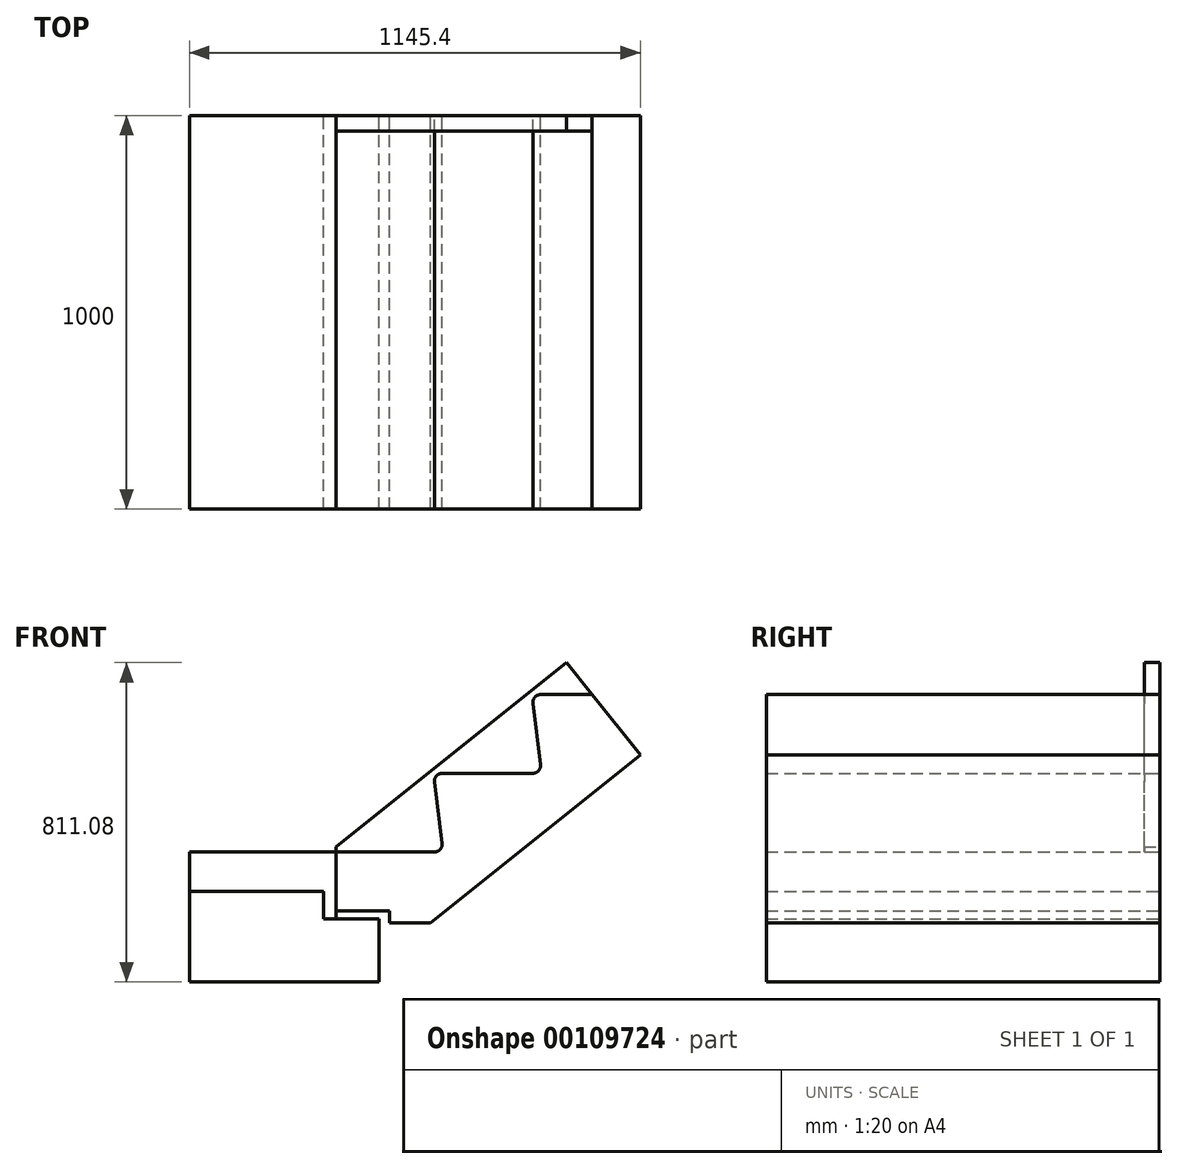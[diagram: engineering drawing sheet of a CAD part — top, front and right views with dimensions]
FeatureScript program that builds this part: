
annotation { "Feature Type Name" : "Feature", "Feature Type Description" : "" }
export const myFeature = defineFeature(function(context is Context, id is Id, definition is map)
    precondition{}
    {
        {
            var Q0;
            Q0=qCreatedBy(makeId("Front.planeOp"),FACE);
            var sketch = newSketch(context, id + "F0", { "sketchPlane" : qUnion([Q0])});
            skLineSegment(sketch, "E0", {"start": v(-200.38, -23.77) * mm, "end": v(49.16, -23.77) * mm});
            skLineSegment(sketch, "E1", {"start": v(69, -1.3) * mm, "end": v(49.62, 153.75) * mm});
            skLineSegment(sketch, "E2", {"start": v(-200.38, -11.26) * mm, "end": v(385.33, 457.31) * mm});
            skLineSegment(sketch, "E3", {"start": v(-90.79, -353.77) * mm, "end": v(-572.74, -353.77) * mm});
            skLineSegment(sketch, "E4", {"start": v(39.21, -203.77) * mm, "end": v(-63.95, -203.77) * mm});
            skLineSegment(sketch, "E5", {"start": v(69.47, 176.23) * mm, "end": v(299.16, 176.23) * mm});
            skLineSegment(sketch, "E6", {"start": v(319, 198.7) * mm, "end": v(299.62, 353.75) * mm});
            skLineSegment(sketch, "E7", {"start": v(319.47, 376.23) * mm, "end": v(450.15, 376.23) * mm});
            skLineSegment(sketch, "E8", {"start": v(-90.79, -193.77) * mm, "end": v(-90.79, -353.77) * mm});
            skLineSegment(sketch, "E9", {"start": v(-232.11, -193.77) * mm, "end": v(-232.11, -123.77) * mm});
            skLineSegment(sketch, "E10", {"start": v(-63.95, -173.77) * mm, "end": v(-200.38, -173.77) * mm});
            skLineSegment(sketch, "E11", {"start": v(-90.79, -193.77) * mm, "end": v(-232.11, -193.77) * mm});
            skLineSegment(sketch, "E12", {"start": v(-200.38, -173.77) * mm, "end": v(-200.38, -23.77) * mm});
            skLineSegment(sketch, "E13", {"start": v(318.48, 540.94) * mm, "end": v(688.52, 78.06) * mm});
            skLineSegment(sketch, "E14", {"start": v(-572.74, 82.67) * mm, "end": v(-572.74, -447.5) * mm});
            skArc(sketch, "E15", {"start": v(49.16, -23.77) * mm, "mid": v(64.15, -17) * mm, "end": v(69, -1.3) * mm});
            skArc(sketch, "E16", {"start": v(69.47, 176.23) * mm, "mid": v(54.48, 169.47) * mm, "end": v(49.62, 153.75) * mm});
            skArc(sketch, "E17", {"start": v(299.16, 176.23) * mm, "mid": v(314.15, 183) * mm, "end": v(319, 198.7) * mm});
            skArc(sketch, "E18", {"start": v(319.47, 376.23) * mm, "mid": v(304.48, 369.47) * mm, "end": v(299.62, 353.75) * mm});
            skLineSegment(sketch, "E19", {"start": v(-90.79, -353.77) * mm, "end": v(650.48, -353.77) * mm});
            skLineSegment(sketch, "E20", {"start": v(226.71, -53.77) * mm, "end": v(650.48, -53.77) * mm});
            skLineSegment(sketch, "E21", {"start": v(650.48, 14.5) * mm, "end": v(650.48, -397.5) * mm});
            skLineSegment(sketch, "E22", {"start": v(39.21, -203.77) * mm, "end": v(572.66, 222.99) * mm});
            skLineSegment(sketch, "E23", {"start": v(-90.79, -303.77) * mm, "end": v(-572.74, -303.77) * mm});
            skLineSegment(sketch, "E24", {"start": v(-63.95, -203.77) * mm, "end": v(-63.95, -173.77) * mm});
            skLineSegment(sketch, "E25", {"start": v(-232.11, -123.77) * mm, "end": v(-572.74, -123.77) * mm});
            skLineSegment(sketch, "E26", {"start": v(-200.38, -23.77) * mm, "end": v(-572.74, -23.77) * mm});
            skLineSegment(sketch, "E27", {"start": v(-200.38, -173.77) * mm, "end": v(-200.38, -193.77) * mm});
            skLineSegment(sketch, "E28", {"start": v(-90.79, -193.77) * mm, "end": v(-90.79, -173.77) * mm});
            skLineSegment(sketch, "E29", {"start": v(-200.38, -173.77) * mm, "end": v(-90.79, -193.77) * mm});
            skLineSegment(sketch, "E30", {"start": v(-90.79, -173.77) * mm, "end": v(-200.38, -193.77) * mm});
            skLineSegment(sketch, "E31", {"start": v(-200.38, -11.26) * mm, "end": v(-200.38, -23.77) * mm});
            skSolve(sketch);
        }
        {
            var Q0;
            {var subQ1=sQuery(id+"F0.wireOp",EDGE,"E9");Q0=makeQuery(id+"F0.imprint","IMPRINT",FACE,{"disambiguationData":[TD([[makeQuery(id+"F0.imprint","IMPRINT",EDGE,{"derivedFrom":subQ1}),1.0]])]});}
            var Q1;
            {var subQ0=sQuery(id+"F0.wireOp",EDGE,"E3");Q1=makeQuery(id+"F0.imprint","IMPRINT",FACE,{"disambiguationData":[TD([[makeQuery(id+"F0.imprint","IMPRINT",EDGE,{"derivedFrom":subQ0}),-1.0]])]});}
            extrude(context, id + "F1", {"entities" : qUnion([Q0, Q1]), "depth" : 1000 * mm});
        }
        {
            var Q0;
            {var subQ4=sQuery(id+"F0.wireOp",EDGE,"E9");Q0=makeQuery(id+"F0.imprint","IMPRINT",FACE,{"disambiguationData":[TD([[makeQuery(id+"F0.imprint","IMPRINT",EDGE,{"derivedFrom":subQ4}),-1.0]])]});}
            extrude(context, id + "F2", {"entities" : qUnion([Q0]), "depth" : 1000 * mm});
        }
        {
            var Q0;
            Q0=makeQuery(id+"F0.imprint","IMPRINT",FACE,{"disambiguationData":[TD([[makeQuery(id+"F0.imprint","IMPRINT",EDGE,{"derivedFrom":sQuery(id+"F0.wireOp",EDGE,"E0")}),-1.0]])]});
            extrude(context, id + "F3", {"entities" : qUnion([Q0]), "depth" : 1000 * mm});
        }
        {
            var Q0;
            Q0=makeQuery(id+"F0.imprint","IMPRINT",FACE,{"disambiguationData":[TD([[makeQuery(id+"F0.imprint","IMPRINT",EDGE,{"derivedFrom":sQuery(id+"F0.wireOp",EDGE,"E0")}),1.0]])]});
            extrude(context, id + "F4", {"entities" : qUnion([Q0]), "depth" : 40 * mm});
        }
    });
